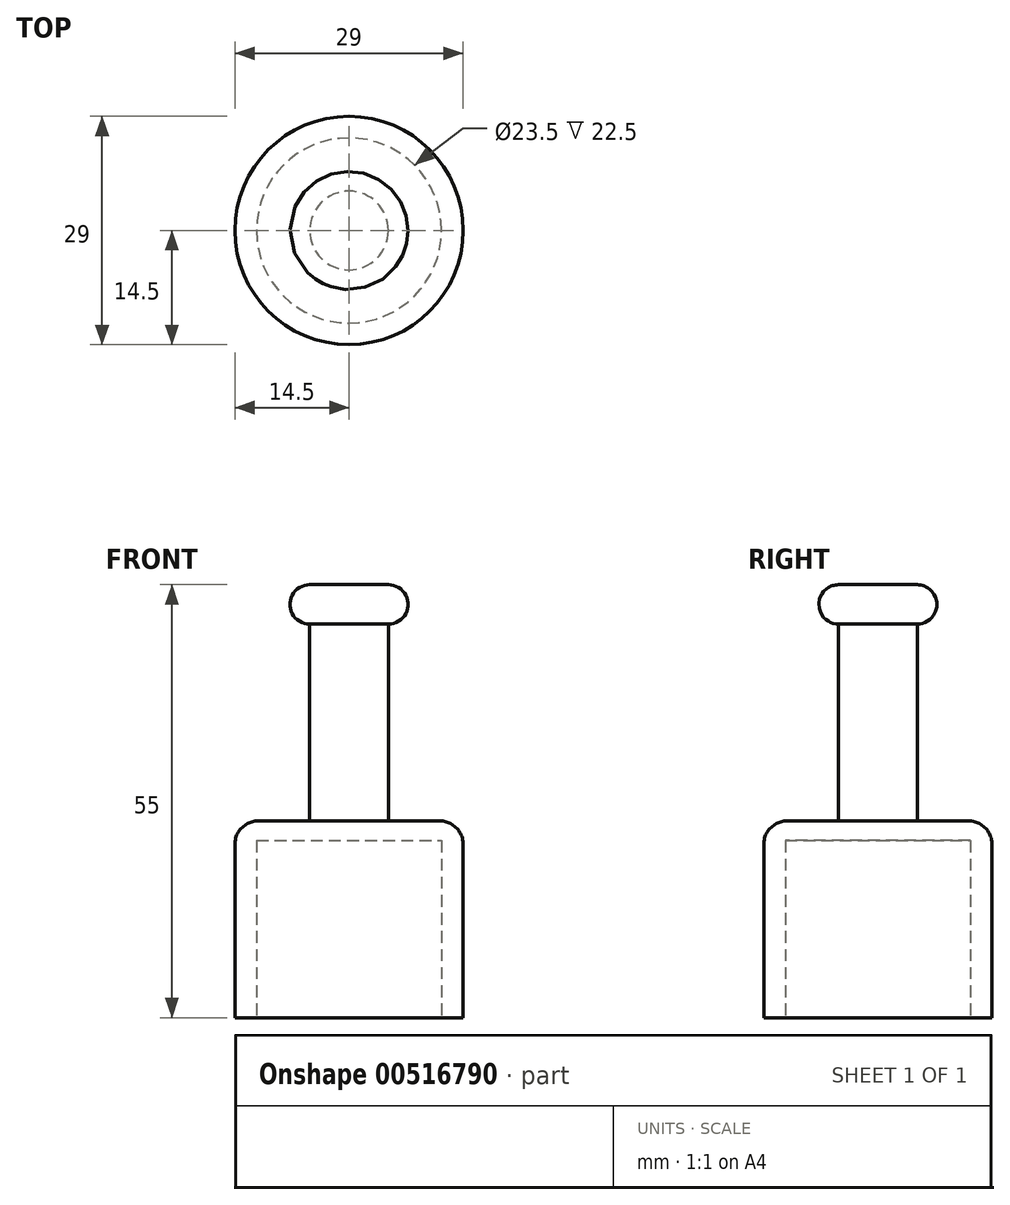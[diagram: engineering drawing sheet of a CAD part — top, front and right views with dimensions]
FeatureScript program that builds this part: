
annotation { "Feature Type Name" : "Feature", "Feature Type Description" : "" }
export const myFeature = defineFeature(function(context is Context, id is Id, definition is map)
    precondition{}
    {
        {
            var Q0;
            Q0=qCreatedBy(makeId("Top.planeOp"),FACE);
            var sketch = newSketch(context, id + "F0", { "sketchPlane" : qUnion([Q0])});
            skCircle(sketch, "E0", {"center": v(0, 0) * mm, "radius": 14.5 * mm});
            skSolve(sketch);
        }
        {
            var Q0;
            Q0 = qSketchRegion(id + "F0", true);
            extrude(context, id + "F1", {"entities" : qUnion([Q0]), "depth" : 25 * mm, "offsetDistance" : 25 * mm});
        }
        {
            var Q0;
            Q0=makeQuery(id+"F1.opExtrude","CAP_FACE",FACE,{"disambiguationData":[OSD([sQuery(id+"F0.wireOp",EDGE,"E0")])],"isStart":false});
            var sketch = newSketch(context, id + "F2", { "sketchPlane" : qUnion([Q0])});
            skCircle(sketch, "E1", {"center": v(0, 0) * mm, "radius": 5 * mm});
            skSolve(sketch);
        }
        {
            var Q0;
            Q0=makeQuery(id+"F2.imprint","IMPRINT",FACE,{"disambiguationData":[TD([[makeQuery(id+"F2.imprint","IMPRINT",EDGE,{"derivedFrom":sQuery(id+"F2.wireOp",EDGE,"E1")}),1.0]])]});
            extrude(context, id + "F3", {"entities" : qUnion([Q0]), "operationType" : NewBodyOperationType.ADD, "depth" : 25 * mm, "offsetDistance" : 25 * mm});
        }
        {
            var Q0;
            Q0=makeQuery(id+"F3.opExtrude","CAP_FACE",FACE,{"disambiguationData":[OSD([sQuery(id+"F2.wireOp",EDGE,"E1")])],"isStart":false});
            var sketch = newSketch(context, id + "F4", { "sketchPlane" : qUnion([Q0])});
            skCircle(sketch, "E2", {"center": v(0, 0) * mm, "radius": 7.5 * mm});
            skSolve(sketch);
        }
        {
            var Q0;
            Q0 = qSketchRegion(id + "F4", true);
            extrude(context, id + "F5", {"entities" : qUnion([Q0]), "operationType" : NewBodyOperationType.ADD, "depth" : 5 * mm, "offsetDistance" : 25 * mm});
        }
        {
            var Q0;
            Q0=makeQuery(id+"F5.opExtrude","CAP_EDGE",EDGE,{"disambiguationData":[OSD([sQuery(id+"F4.wireOp",EDGE,"E2")])],"isStart":true});
            var Q1;
            Q1=makeQuery(id+"F5.opExtrude","CAP_EDGE",EDGE,{"disambiguationData":[OSD([sQuery(id+"F4.wireOp",EDGE,"E2")])],"isStart":false});
            fillet(context, id + "F6", {"entities" : qUnion([Q0, Q1]), "radius" : 2.5 * mm, "tangentPropagation" : true, "allowEdgeOverflow" : false});
        }
        {
            var Q0;
            Q0=makeQuery(id+"F1.opExtrude","CAP_EDGE",EDGE,{"disambiguationData":[OSD([sQuery(id+"F0.wireOp",EDGE,"E0")])],"isStart":false});
            fillet(context, id + "F7", {"entities" : qUnion([Q0]), "radius" : 3 * mm, "tangentPropagation" : true, "allowEdgeOverflow" : false});
        }
        {
            var Q0;
            Q0=makeQuery(id+"F1.opExtrude","CAP_FACE",FACE,{"disambiguationData":[OSD([sQuery(id+"F0.wireOp",EDGE,"E0")])],"isStart":true});
            var sketch = newSketch(context, id + "F8", { "sketchPlane" : qUnion([Q0])});
            skCircle(sketch, "E3", {"center": v(0, 0) * mm, "radius": 11.75 * mm});
            skSolve(sketch);
        }
        {
            var Q0;
            Q0 = qSketchRegion(id + "F8", true);
            extrude(context, id + "F9", {"entities" : qUnion([Q0]), "operationType" : NewBodyOperationType.REMOVE, "oppositeDirection" : true, "depth" : 22.5 * mm, "offsetDistance" : 25 * mm});
        }
    });
